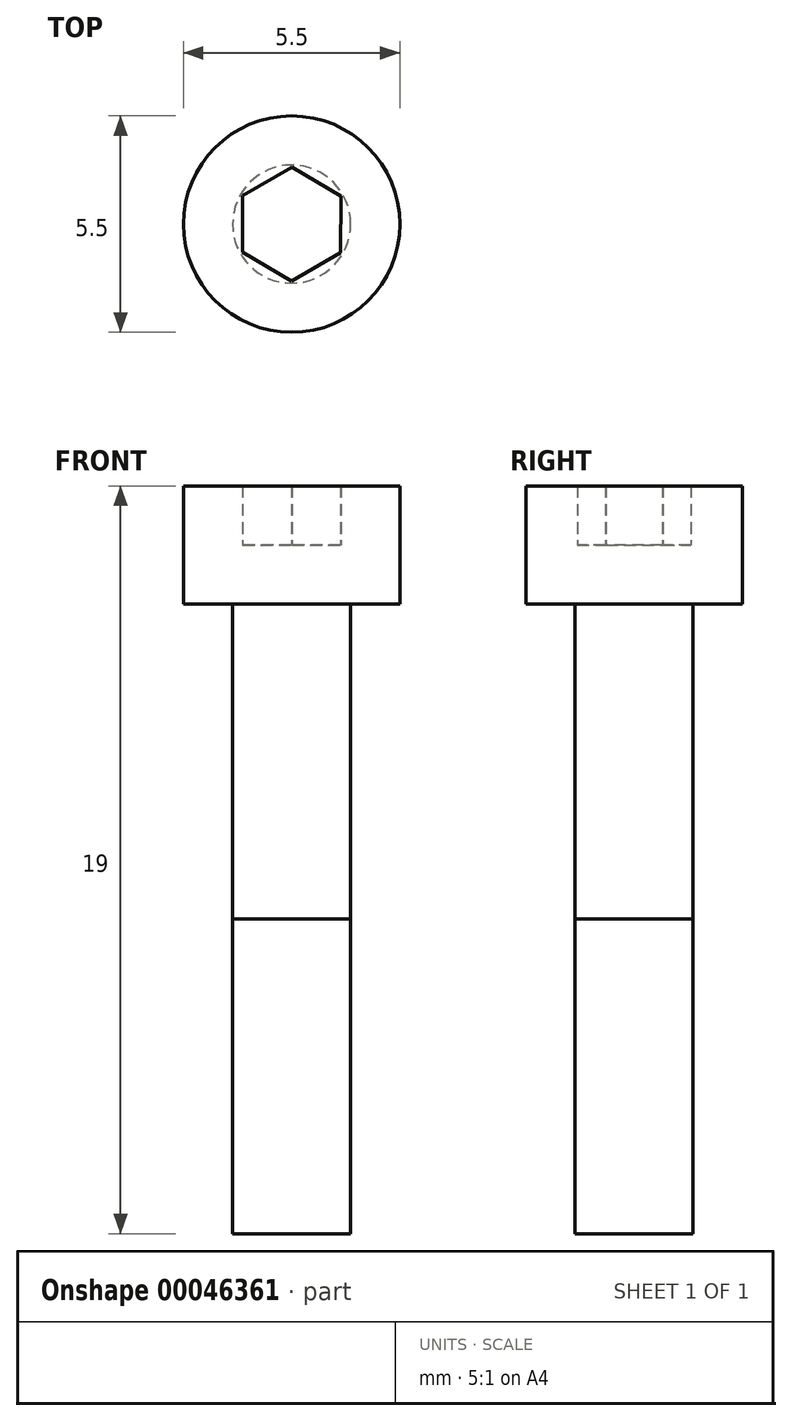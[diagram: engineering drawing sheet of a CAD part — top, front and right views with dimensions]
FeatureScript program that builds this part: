
annotation { "Feature Type Name" : "Feature", "Feature Type Description" : "" }
export const myFeature = defineFeature(function(context is Context, id is Id, definition is map)
    precondition{}
    {
        {
            var Q0;
            Q0=qCreatedBy(makeId("Top.planeOp"),FACE);
            var sketch = newSketch(context, id + "F0", { "sketchPlane" : qUnion([Q0])});
            skCircle(sketch, "E0", {"center": v(0, 0) * mm, "radius": 1.5 * mm});
            skCircle(sketch, "E1", {"center": v(0, 0) * mm, "radius": 2.75 * mm});
            skCircle(sketch, "E2.cCircle", {"center": v(0, 0) * mm, "radius": 1.44 * mm, "construction": true});
            skLineSegment(sketch, "E2.0", {"start": v(1.25, -0.73) * mm, "end": v(0, -1.44) * mm});
            skLineSegment(sketch, "E2.1", {"start": v(0, -1.44) * mm, "end": v(-1.25, -0.72) * mm});
            skLineSegment(sketch, "E2.2", {"start": v(-1.25, -0.72) * mm, "end": v(-1.25, 0.73) * mm});
            skLineSegment(sketch, "E2.3", {"start": v(-1.25, 0.73) * mm, "end": v(0, 1.44) * mm});
            skLineSegment(sketch, "E2.4", {"start": v(0, 1.44) * mm, "end": v(1.25, 0.72) * mm});
            skLineSegment(sketch, "E2.5", {"start": v(1.25, 0.72) * mm, "end": v(1.25, -0.73) * mm});
            skSolve(sketch);
        }
        {
            var Q0;
            Q0=makeQuery(id+"F0.imprint","IMPRINT",FACE,{"disambiguationData":[TD([[makeQuery(id+"F0.imprint","IMPRINT",EDGE,{"derivedFrom":sQuery(id+"F0.wireOp",EDGE,"E0")}),-1.0]])]});
            var Q1;
            Q1=makeQuery(id+"F0.imprint","IMPRINT",FACE,{"disambiguationData":[TD([[makeQuery(id+"F0.imprint","IMPRINT",EDGE,{"derivedFrom":sQuery(id+"F0.wireOp",EDGE,"E0")}),1.0]])]});
            extrude(context, id + "F1", {"entities" : qUnion([Q0, Q1]), "depth" : 3 * mm});
        }
        {
            var Q0;
            Q0=makeQuery(id+"F0.imprint","IMPRINT",FACE,{"disambiguationData":[TD([[makeQuery(id+"F0.imprint","IMPRINT",EDGE,{"derivedFrom":sQuery(id+"F0.wireOp",EDGE,"E2.0")}),-1.0]])]});
            extrude(context, id + "F2", {"entities" : qUnion([Q0]), "operationType" : NewBodyOperationType.ADD, "depth" : 1.5 * mm});
        }
        {
            var Q0;
            Q0=makeQuery(id+"F0.imprint","IMPRINT",FACE,{"disambiguationData":[TD([[makeQuery(id+"F0.imprint","IMPRINT",EDGE,{"derivedFrom":sQuery(id+"F0.wireOp",EDGE,"E0")}),1.0]])]});
            var Q1;
            Q1=makeQuery(id+"F0.imprint","IMPRINT",FACE,{"disambiguationData":[TD([[makeQuery(id+"F0.imprint","IMPRINT",EDGE,{"derivedFrom":sQuery(id+"F0.wireOp",EDGE,"E2.0")}),-1.0]])]});
            extrude(context, id + "F3", {"entities" : qUnion([Q0, Q1]), "oppositeDirection" : true, "depth" : 16 * mm});
        }
        {
            var Q0;
            Q0=makeQuery(id+"F0.imprint","IMPRINT",FACE,{"disambiguationData":[TD([[makeQuery(id+"F0.imprint","IMPRINT",EDGE,{"derivedFrom":sQuery(id+"F0.wireOp",EDGE,"E2.0")}),-1.0]])]});
            var Q1;
            Q1=makeQuery(id+"F0.imprint","IMPRINT",FACE,{"disambiguationData":[TD([[makeQuery(id+"F0.imprint","IMPRINT",EDGE,{"derivedFrom":sQuery(id+"F0.wireOp",EDGE,"E0")}),1.0]])]});
            extrude(context, id + "F4", {"entities" : qUnion([Q0, Q1]), "oppositeDirection" : true, "depth" : 8 * mm});
        }
        {
            var Q0;
            Q0=makeQuery(id+"F1.opExtrude","SWEPT_BODY",BODY,{"disambiguationData":[OSD([sQuery(id+"F0.wireOp",EDGE,"E1"),sQuery(id+"F0.wireOp",EDGE,"E2.0"),sQuery(id+"F0.wireOp",EDGE,"E2.1"),sQuery(id+"F0.wireOp",EDGE,"E2.2"),sQuery(id+"F0.wireOp",EDGE,"E2.3"),sQuery(id+"F0.wireOp",EDGE,"E2.4"),sQuery(id+"F0.wireOp",EDGE,"E2.5")])]});
            transform(context, id + "F5", {"entities" : qUnion([Q0]), "transformType" : TransformType.TRANSLATION_3D, "dx" : 0 * mm, "dy" : 0 * mm, "dz" : 0 * mm, "makeCopy" : true});
        }
        {
            var Q0;
            Q0=makeQuery(id+"F5.opPattern","COPY",BODY,{"derivedFrom":makeQuery(id+"F1.opExtrude","SWEPT_BODY",BODY,{"disambiguationData":[OSD([sQuery(id+"F0.wireOp",EDGE,"E1"),sQuery(id+"F0.wireOp",EDGE,"E2.0"),sQuery(id+"F0.wireOp",EDGE,"E2.1"),sQuery(id+"F0.wireOp",EDGE,"E2.2"),sQuery(id+"F0.wireOp",EDGE,"E2.3"),sQuery(id+"F0.wireOp",EDGE,"E2.4"),sQuery(id+"F0.wireOp",EDGE,"E2.5")])]}),"instanceName":"1"});
            transform(context, id + "F6", {"entities" : qUnion([Q0]), "transformType" : TransformType.TRANSLATION_3D, "dx" : 0 * mm, "dy" : 0 * mm, "dz" : 0 * mm, "makeCopy" : true});
        }
    });
